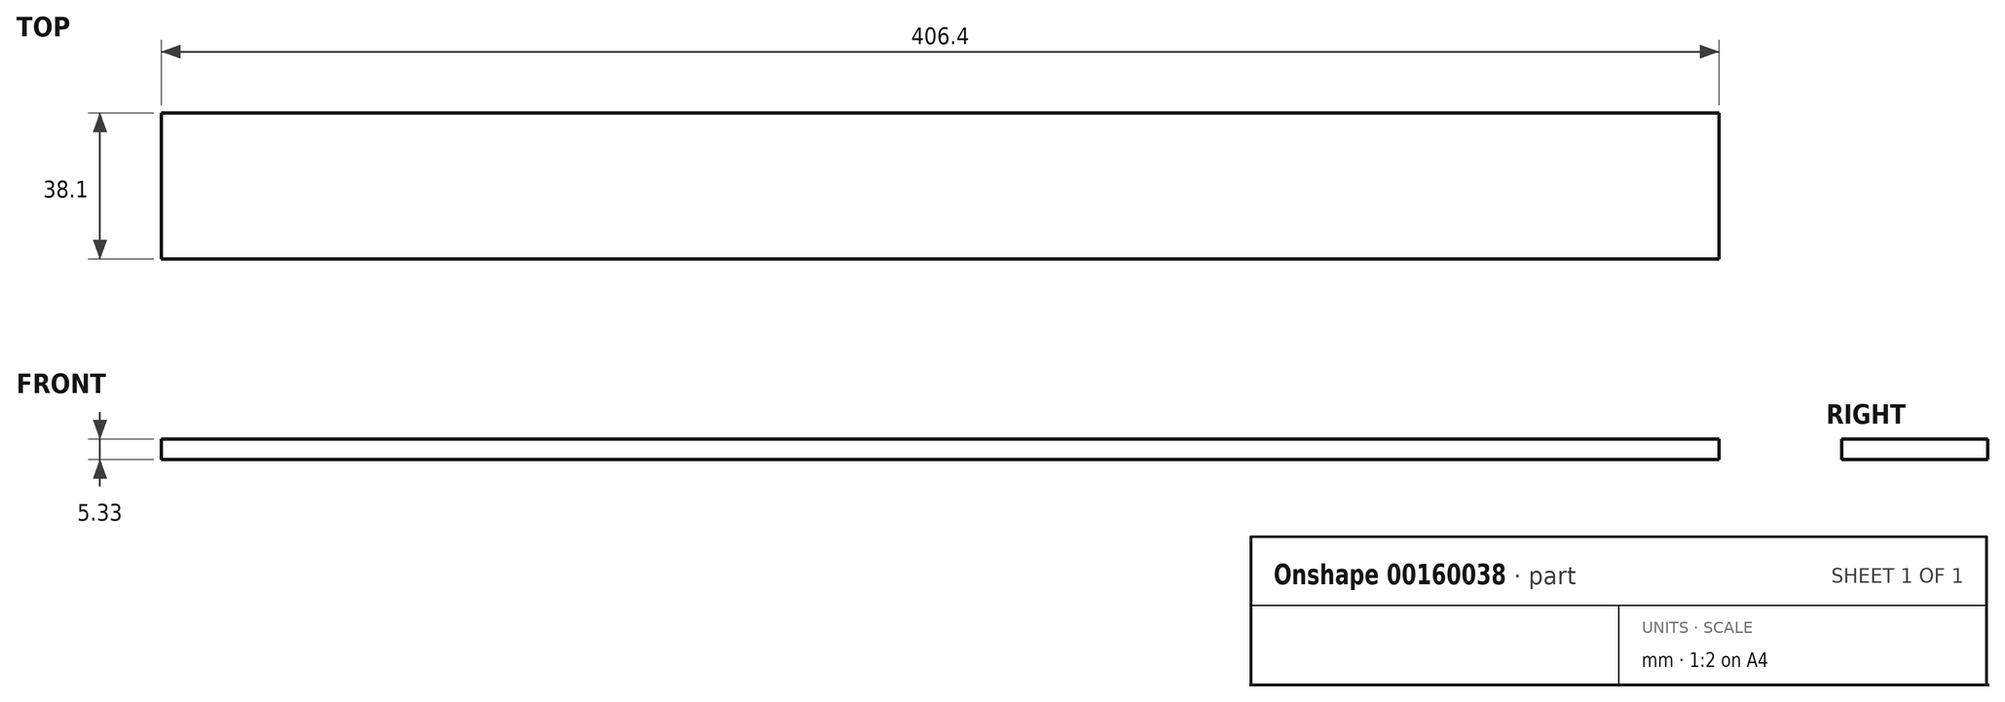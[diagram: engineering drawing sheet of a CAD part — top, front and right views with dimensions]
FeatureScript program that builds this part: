
annotation { "Feature Type Name" : "Feature", "Feature Type Description" : "" }
export const myFeature = defineFeature(function(context is Context, id is Id, definition is map)
    precondition{}
    {
        {
            var Q0;
            Q0=qCreatedBy(makeId("Top.planeOp"),FACE);
            var sketch = newSketch(context, id + "F0", { "sketchPlane" : qUnion([Q0])});
            skLineSegment(sketch, "E0.bottom", {"start": v(0, 0) * mm, "end": v(406.4, 0) * mm});
            skLineSegment(sketch, "E0.top", {"start": v(0, 38.1) * mm, "end": v(406.4, 38.1) * mm});
            skLineSegment(sketch, "E0.left", {"start": v(0, 0) * mm, "end": v(0, 38.1) * mm});
            skLineSegment(sketch, "E0.right", {"start": v(406.4, 0) * mm, "end": v(406.4, 38.1) * mm});
            skSolve(sketch);
        }
        {
            var Q0;
            Q0 = qSketchRegion(id + "F0", true);
            extrude(context, id + "F1", {"entities" : qUnion([Q0]), "depth" : 5.33 * mm});
        }
    });
